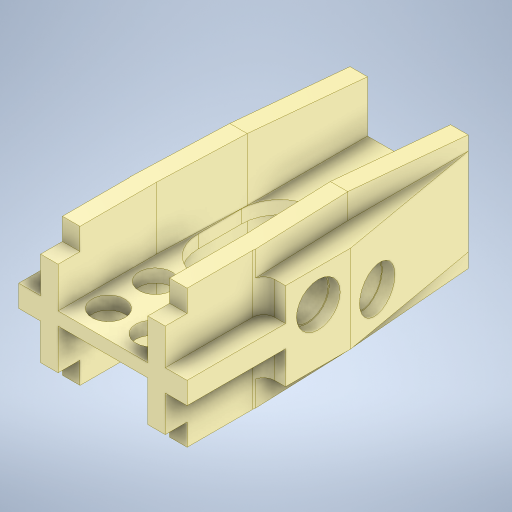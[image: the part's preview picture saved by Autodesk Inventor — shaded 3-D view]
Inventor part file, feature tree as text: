
AUTODESK INVENTOR PART (.ipt)
format: ipt  version: 2023.5 (Build 275446020, 446B)  size: 563,712 bytes
history: native  units: mm
features: extrude x13, other x6, fillet x2, mirror x2, pattern_linear x1, pattern_circular x1
ambient origin geometry x8: Origin, YZ Plane, XZ Plane, XY Plane, X Axis, Y Axis, Z Axis, Center Point
bodies: Solid1 (feature_tree)
feature tree (25):
  other  "Sk:Base"
  extrude  "Ex:Midline"  Depth=2.05mm
  extrude  "Ex:FrontSupport"  Depth=4.5mm
  extrude  "Ex:SideRidge"  TaperAngle=0.0deg  [1 undecoded]
  extrude  "Ex:SideWall"  Depth=1.9mm
  extrude  "Ex:BaseHole"  TaperAngle=0.0deg  [1 undecoded]
  pattern_linear  "Pat:BaseHoles"  Spacing1=0.0mm  [1 undecoded]
  extrude  "Ex:RemMaterial"  Depth=3.15mm TaperAngle=0.0deg
  fillet  "Fillet:Support"  Radius=0.8mm
  extrude  "Ex:Widening"  Depth=2.25mm
  fillet  "Fillet:Side"  Radius=4.0mm
  extrude  "Ex:FrontTaper"  Depth=1.5mm
  extrude  "Ex:LidNotch"  Depth=1.25mm
  mirror  "Mirror1"
  mirror  "Mirror2"
  other  "Sk:ThreadHole1"
  other  "Sk:ThreadHole2"
  extrude  "Ex:ThreadHole1"  Depth=5.3mm TaperAngle=0.0deg
  extrude  "Ex:ThreadHole2"  Depth=40.0mm
  extrude  "Ex:ThreadEntry1"  Depth=1.0mm
  extrude  "Ex:ThreadEntry2"  Depth=1.75mm
  pattern_circular  "Pat:Threads"  [2 undecoded]
  other  "Sk:BaseHole"
  other  "Sk:FrontTaper"
  other  "Sk:LidNotch"
note: 5 required parameter values undecoded (feature->parameter linkage not recoverable at this tier; creation-order binding heuristic only, values carry confidence <= 0.55)
